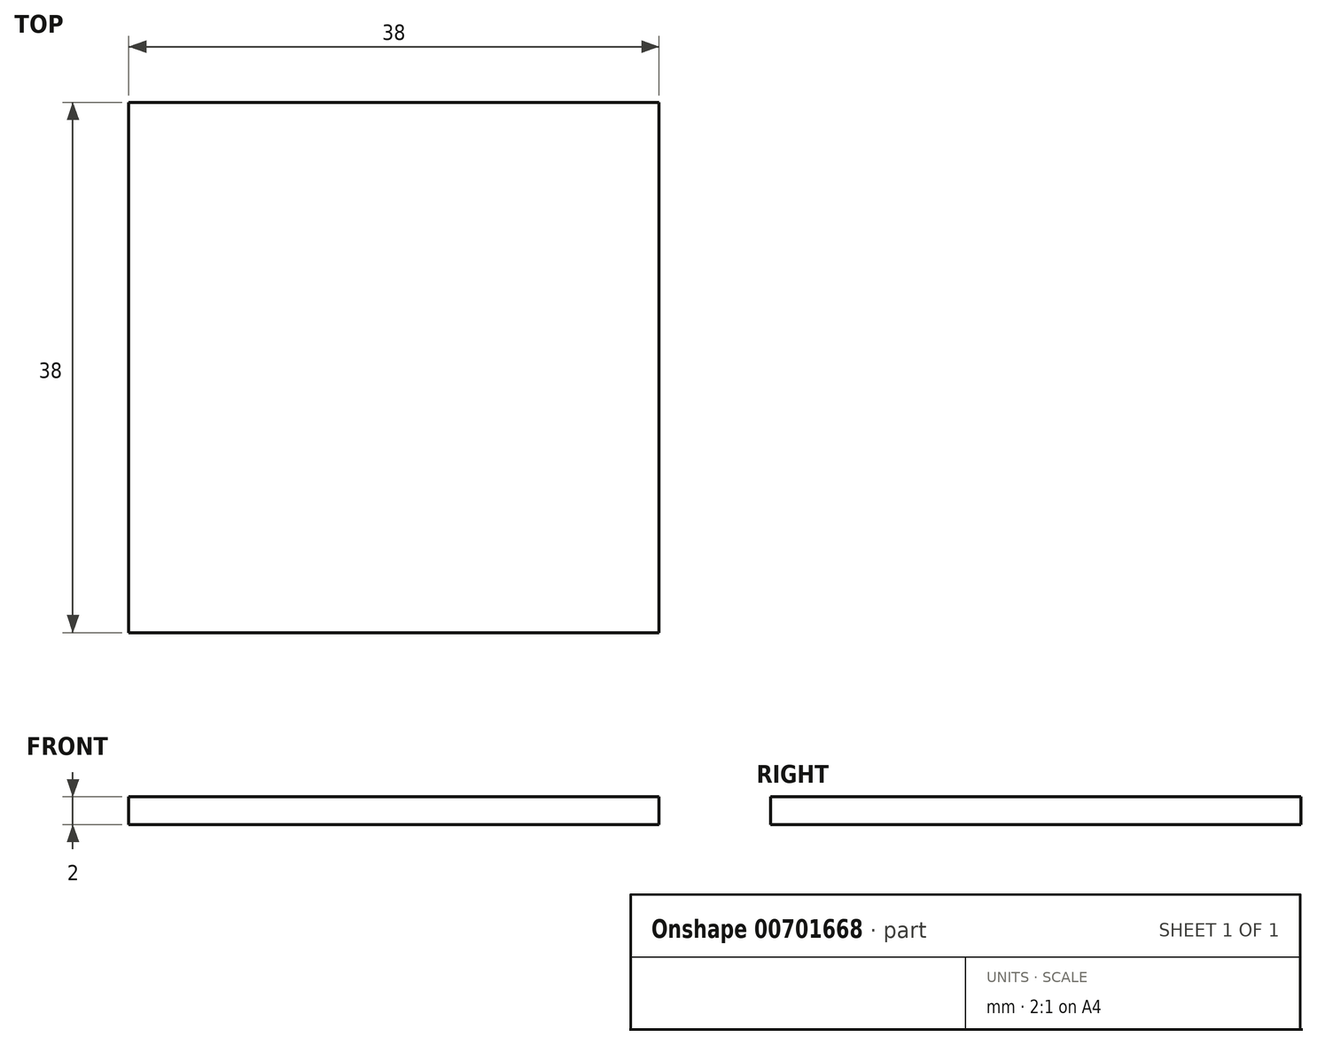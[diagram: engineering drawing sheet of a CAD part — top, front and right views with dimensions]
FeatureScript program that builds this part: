
annotation { "Feature Type Name" : "Feature", "Feature Type Description" : "" }
export const myFeature = defineFeature(function(context is Context, id is Id, definition is map)
    precondition{}
    {
        {
            var Q0;
            Q0=qCreatedBy(makeId("Top.planeOp"),FACE);
            var sketch = newSketch(context, id + "F0", { "sketchPlane" : qUnion([Q0])});
            skLineSegment(sketch, "E0.bottom", {"start": v(19, 19) * mm, "end": v(-19, 19) * mm});
            skLineSegment(sketch, "E0.top", {"start": v(19, -19) * mm, "end": v(-19, -19) * mm});
            skLineSegment(sketch, "E0.left", {"start": v(19, 19) * mm, "end": v(19, -19) * mm});
            skLineSegment(sketch, "E0.right", {"start": v(-19, 19) * mm, "end": v(-19, -19) * mm});
            skPoint(sketch, "E0.middle", {"position": v(0, 0) * mm});
            skSolve(sketch);
        }
        {
            var Q0;
            Q0=makeQuery(id+"F0.imprint","IMPRINT",FACE,{"disambiguationData":[TD([[makeQuery(id+"F0.imprint","IMPRINT",EDGE,{"derivedFrom":sQuery(id+"F0.wireOp",EDGE,"E0.bottom")}),1.0]])]});
            extrude(context, id + "F1", {"entities" : qUnion([Q0]), "depth" : 2 * mm, "offsetDistance" : 25 * mm});
        }
    });
